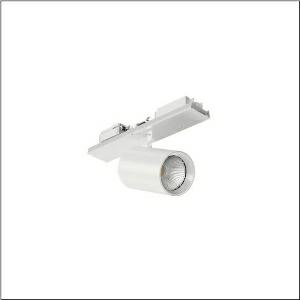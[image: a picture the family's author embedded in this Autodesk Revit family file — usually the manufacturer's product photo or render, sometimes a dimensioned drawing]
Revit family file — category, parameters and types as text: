
# Revit family: licross_r__spot_31_51sl127a45b_74df
name_source: partatom
category: Lighting Fixtures
units: mm (PartAtom-declared; Revit-internal decimal feet)

## family parameters
Cut with Voids When Loaded = No
Host = Face
Light Source = No
Part Type = Normal
Room Calculation Point = No
Round Connector Dimension = Use Diameter
Shared = No

## types (1)
- --- (1 x LED, 5140 lm, 42.6 W, 4000K)
    Apparent Load = 43 VA
    CIE Flux Codes = 93 97 99 100 100
    Color Rendering = 90
    Color Temperature = 4000K
    Default Elevation = 1800 mm
    Description = Licross® Spot 31, directional spotlight, light control with lens, of plastic, LED rated luminous flux: 5.140lm, light colour: 940, with plug, 3-pole, with phase selection, mains connection: 220..240V, AC, 50/60Hz, of aluminium, traffic white (RAL 9016), length: 300mm, diameter: 90mm, protection rating (complete): IP20, insulation class (complete): insulation class I (protective earthing), certification: CE, packaging unit: 1 piece
    Height = 175 mm
    Lamp = 1 x LED
    Lamp Light Flux = 5140 lm
    Lamp Power = 42.6 W
    Lamp count = 1
    Length = 90 mm
    Luminous efficacy = 121 lm/W
    Manufacturer = Siteco
    ModVariant = No
    Model = 51SL127A45B
    Mounting Place = Ceiling
    Mounting Type = Pendant
    Number of Poles = 1
    OnlyDefault = Yes
    Power Factor = 1
    Product Name = Licross® Spot 31
    Product group = directional spotlight
    ProductGroupID = 906
    Protection Class = Protection class I
    Protection Degree = IP 20
    RLX_Detail_Level = 1
    RLX_Emergency_Light_Flux = 0 lm
    RLX_Emergency_Type = 0
    RLX_Emergency_Type_DB = No
    RlxData = <blob elided: 14805 chars, md5=202b8d1d>
    Socket = socket
    Standby Power = 0 W
    System Light Flux = 5140 lm
    System Power = 43 W
    Type Comments = factory setting: luminous flux: 100 % | (ON | ON | ON) | 1050 mA
    Type Image = l_1245720.jpg
    URL = http://relux.com
    VarID = @adj_132712
    Voltage = 0 V
    Weight = 0.00 kg
    Width = 0 mm  [stored 0 ft]

note: [stored X ft] marks values corroborated as IEEE doubles in the binary element streams (Revit-internal decimal feet)

## geometry (parser evidence)
native form markers: Sweep x11
no freeform markers — native parametric forms only
